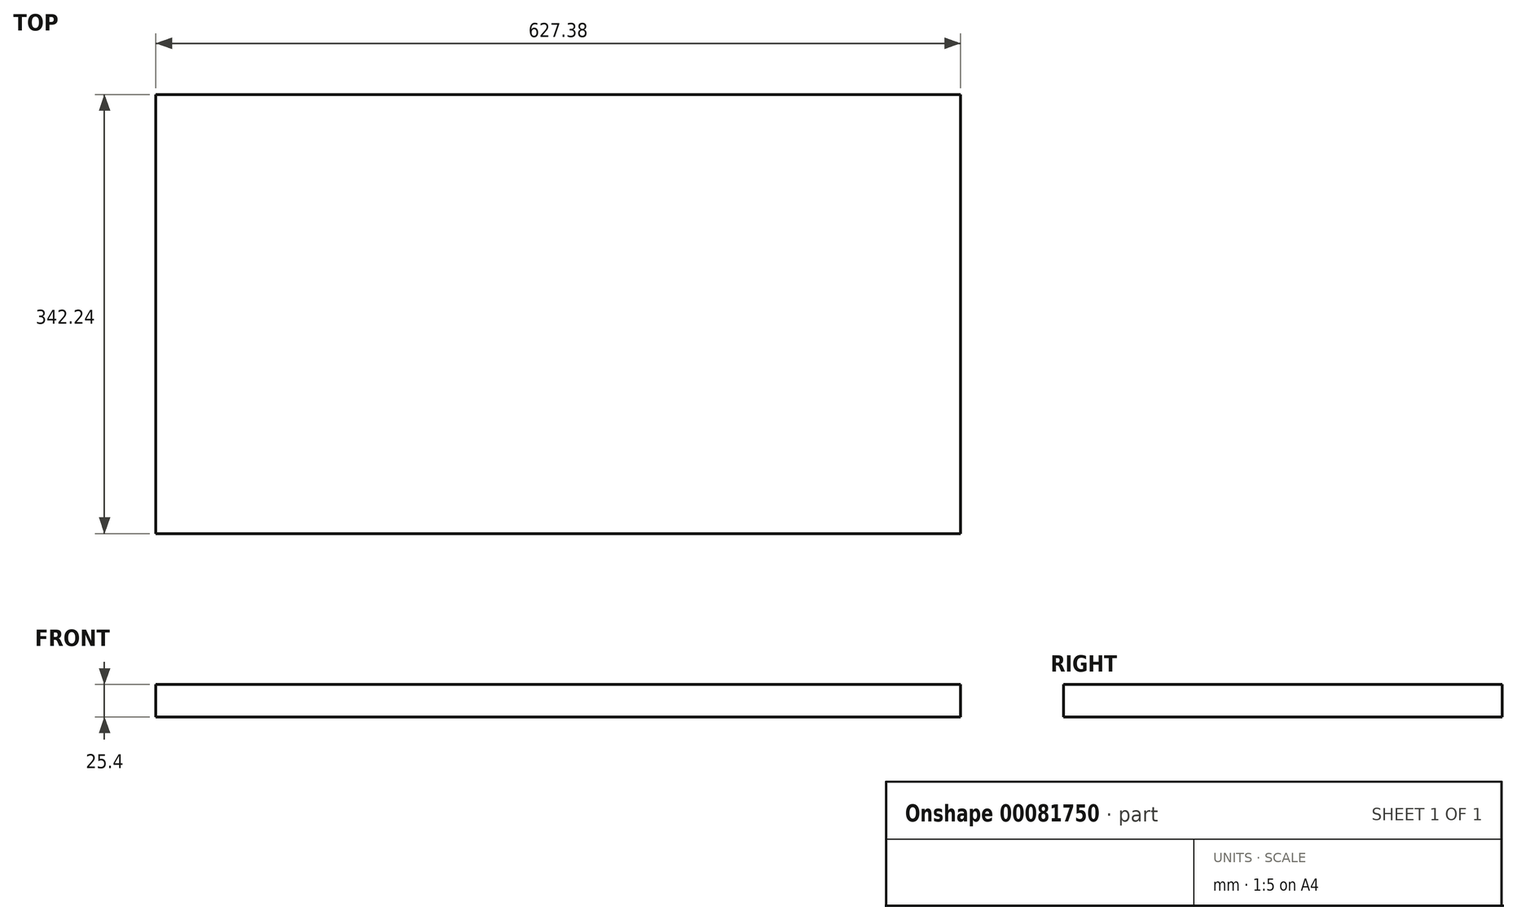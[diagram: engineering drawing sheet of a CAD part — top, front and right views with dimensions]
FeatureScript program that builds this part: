
annotation { "Feature Type Name" : "Feature", "Feature Type Description" : "" }
export const myFeature = defineFeature(function(context is Context, id is Id, definition is map)
    precondition{}
    {
        {
            var Q0;
            Q0=qCreatedBy(makeId("Top.planeOp"),FACE);
            var sketch = newSketch(context, id + "F0", { "sketchPlane" : qUnion([Q0])});
            skLineSegment(sketch, "E0.bottom", {"start": v(-340.94, 155.47) * mm, "end": v(286.44, 155.47) * mm});
            skLineSegment(sketch, "E0.top", {"start": v(-340.94, -186.77) * mm, "end": v(286.44, -186.77) * mm});
            skLineSegment(sketch, "E0.left", {"start": v(-340.94, 155.47) * mm, "end": v(-340.94, -186.77) * mm});
            skLineSegment(sketch, "E0.right", {"start": v(286.44, 155.47) * mm, "end": v(286.44, -186.77) * mm});
            skSolve(sketch);
        }
        {
            var Q0;
            Q0 = qSketchRegion(id + "F0", true);
            extrude(context, id + "F1", {"entities" : qUnion([Q0]), "depth" : 25.4 * mm, "offsetDistance" : 25.4 * mm});
        }
    });
